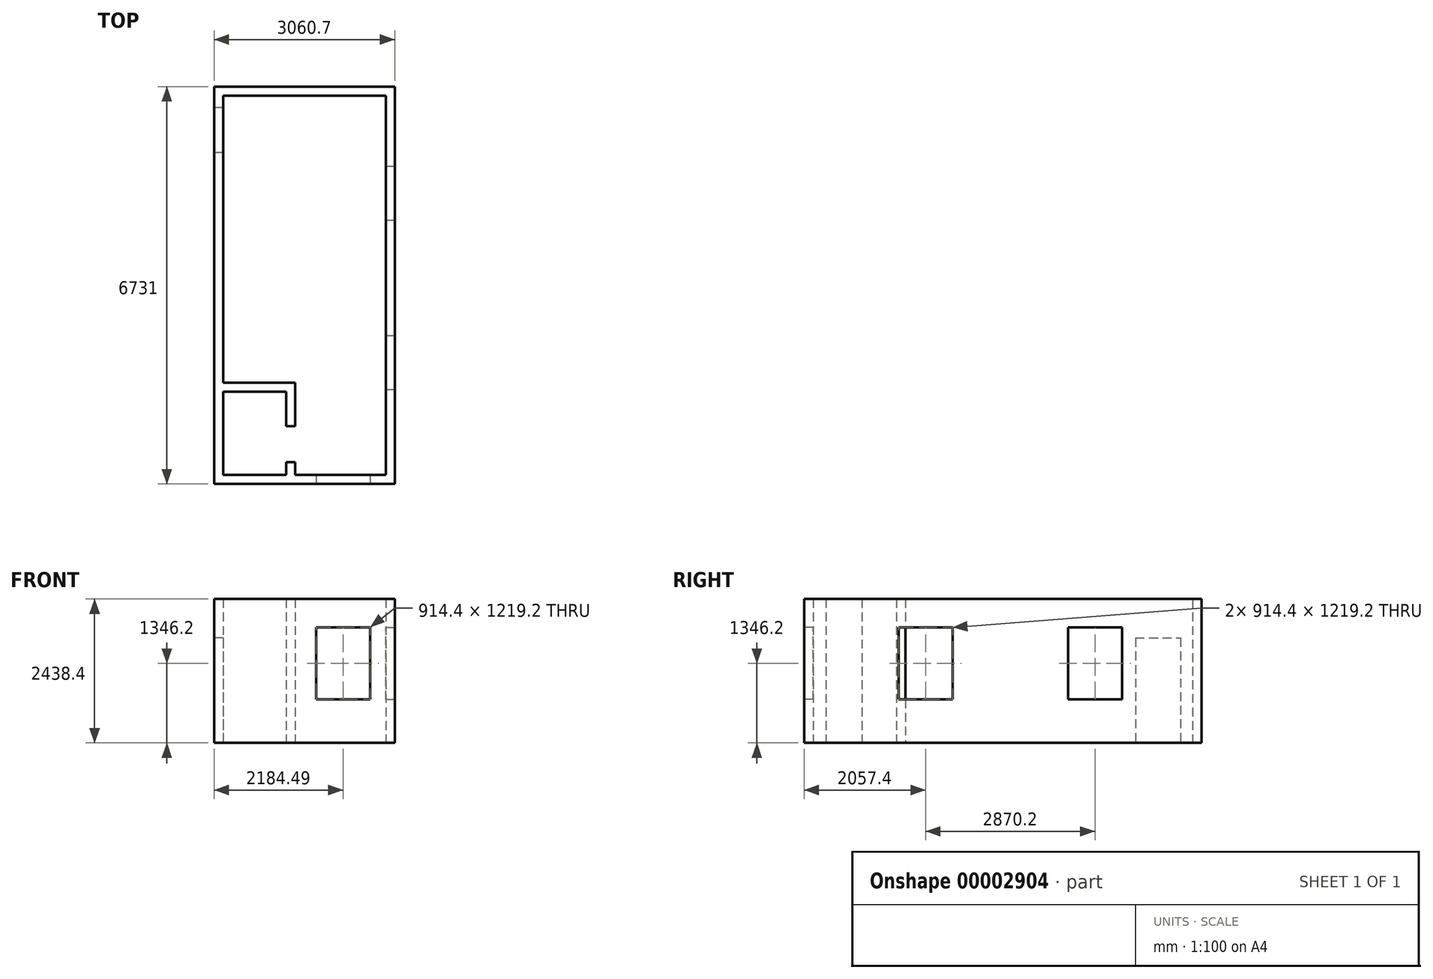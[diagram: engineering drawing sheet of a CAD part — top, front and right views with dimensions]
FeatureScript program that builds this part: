
annotation { "Feature Type Name" : "Feature", "Feature Type Description" : "" }
export const myFeature = defineFeature(function(context is Context, id is Id, definition is map)
    precondition{}
    {
        {
            var Q0;
            Q0=qCreatedBy(makeId("Top.planeOp"),FACE);
            var sketch = newSketch(context, id + "F0", { "sketchPlane" : qUnion([Q0])});
            skLineSegment(sketch, "E0", {"start": v(-1367.03, 42.73) * mm, "end": v(1388.87, 42.73) * mm});
            skLineSegment(sketch, "E1", {"start": v(1388.87, 42.73) * mm, "end": v(1388.87, -6383.47) * mm});
            skLineSegment(sketch, "E2", {"start": v(-1367.03, 42.73) * mm, "end": v(-1367.03, -160.47) * mm});
            skLineSegment(sketch, "E3", {"start": v(1388.87, -6383.47) * mm, "end": v(-147.83, -6383.47) * mm});
            skLineSegment(sketch, "E4.0", {"start": v(-1519.43, 195.13) * mm, "end": v(-1519.43, -160.47) * mm});
            skLineSegment(sketch, "E4.1", {"start": v(-1519.43, 195.13) * mm, "end": v(1541.27, 195.13) * mm});
            skLineSegment(sketch, "E4.2", {"start": v(1541.27, 195.13) * mm, "end": v(1541.27, -6535.87) * mm});
            skLineSegment(sketch, "E4.3", {"start": v(1541.27, -6535.87) * mm, "end": v(-1519.43, -6535.87) * mm});
            skLineSegment(sketch, "E5", {"start": v(-1519.43, -160.47) * mm, "end": v(-1367.03, -160.47) * mm});
            skLineSegment(sketch, "E6", {"start": v(-1519.43, -922.47) * mm, "end": v(-1367.03, -922.47) * mm});
            skLineSegment(sketch, "E7.trimOffspring", {"start": v(-1519.43, -922.47) * mm, "end": v(-1519.43, -6535.87) * mm});
            skLineSegment(sketch, "E8.trimOffspring", {"start": v(-1367.03, -922.47) * mm, "end": v(-1367.03, -4821.37) * mm});
            skLineSegment(sketch, "E9", {"start": v(-1367.03, -4821.37) * mm, "end": v(-147.83, -4821.37) * mm});
            skLineSegment(sketch, "E10", {"start": v(-147.83, -4821.37) * mm, "end": v(-147.83, -5557.97) * mm});
            skLineSegment(sketch, "E11.0", {"start": v(-300.23, -4973.77) * mm, "end": v(-300.23, -5557.97) * mm});
            skLineSegment(sketch, "E11.1", {"start": v(-1367.03, -4973.77) * mm, "end": v(-300.23, -4973.77) * mm});
            skLineSegment(sketch, "E12.trimOffspring", {"start": v(-1367.03, -4973.77) * mm, "end": v(-1367.03, -6383.47) * mm});
            skLineSegment(sketch, "E13.trimOffspring", {"start": v(-300.23, -6383.47) * mm, "end": v(-1367.03, -6383.47) * mm});
            skLineSegment(sketch, "E14", {"start": v(-300.23, -6167.57) * mm, "end": v(-147.83, -6167.57) * mm});
            skLineSegment(sketch, "E15", {"start": v(-147.83, -5557.97) * mm, "end": v(-300.23, -5557.97) * mm});
            skLineSegment(sketch, "E16.trimOffspring", {"start": v(-300.23, -6167.57) * mm, "end": v(-300.23, -6383.47) * mm});
            skLineSegment(sketch, "E17.trimOffspring", {"start": v(-147.83, -6167.57) * mm, "end": v(-147.83, -6383.47) * mm});
            skPoint(sketch, "E18.orphan", {"position": v(0, -5557.97) * mm});
            skPoint(sketch, "E19.orphan", {"position": v(0, -6167.57) * mm});
            skSolve(sketch);
        }
        {
            var Q0;
            Q0=makeQuery(id+"F0.imprint","IMPRINT",FACE,{"disambiguationData":[TD([[makeQuery(id+"F0.imprint","IMPRINT",EDGE,{"derivedFrom":sQuery(id+"F0.wireOp",EDGE,"E0")}),1.0]])]});
            extrude(context, id + "F1", {"entities" : qUnion([Q0]), "depth" : 2438.4 * mm});
        }
        {
            var Q0;
            Q0=makeQuery(id+"F1.opExtrude","SWEPT_FACE",FACE,{"disambiguationData":[OSD([sQuery(id+"F0.wireOp",EDGE,"E4.2")])]});
            var sketch = newSketch(context, id + "F2", { "sketchPlane" : qUnion([Q0])});
            skLineSegment(sketch, "E20.bottom", {"start": v(-1151.07, 1955.8) * mm, "end": v(-2065.47, 1955.8) * mm});
            skLineSegment(sketch, "E20.top", {"start": v(-1151.07, 736.6) * mm, "end": v(-2065.47, 736.6) * mm});
            skLineSegment(sketch, "E20.left", {"start": v(-1151.07, 1955.8) * mm, "end": v(-1151.07, 736.6) * mm});
            skLineSegment(sketch, "E20.right", {"start": v(-2065.47, 1955.8) * mm, "end": v(-2065.47, 736.6) * mm});
            skLineSegment(sketch, "E21.bottom", {"start": v(-4021.27, 1955.8) * mm, "end": v(-4935.67, 1955.8) * mm});
            skLineSegment(sketch, "E21.top", {"start": v(-4021.27, 736.6) * mm, "end": v(-4935.67, 736.6) * mm});
            skLineSegment(sketch, "E21.left", {"start": v(-4021.27, 1955.8) * mm, "end": v(-4021.27, 736.6) * mm});
            skLineSegment(sketch, "E21.right", {"start": v(-4935.67, 1955.8) * mm, "end": v(-4935.67, 736.6) * mm});
            skSolve(sketch);
        }
        {
            var Q0;
            Q0=makeQuery(id+"F2.imprint","IMPRINT",FACE,{"disambiguationData":[TD([[makeQuery(id+"F2.imprint","IMPRINT",EDGE,{"derivedFrom":sQuery(id+"F2.wireOp",EDGE,"E20.bottom")}),1.0]])]});
            var Q1;
            Q1=makeQuery(id+"F2.imprint","IMPRINT",FACE,{"disambiguationData":[TD([[makeQuery(id+"F2.imprint","IMPRINT",EDGE,{"derivedFrom":sQuery(id+"F2.wireOp",EDGE,"E21.bottom")}),1.0]])]});
            extrude(context, id + "F3", {"entities" : qUnion([Q0, Q1]), "operationType" : NewBodyOperationType.REMOVE, "endBound" : BoundingType.UP_TO_NEXT, "oppositeDirection" : true, "depth" : 25.4 * mm});
        }
        {
            var Q0;
            Q0=makeQuery(id+"F1.opExtrude","SWEPT_FACE",FACE,{"disambiguationData":[OSD([sQuery(id+"F0.wireOp",EDGE,"E4.3")])]});
            var sketch = newSketch(context, id + "F4", { "sketchPlane" : qUnion([Q0])});
            skLineSegment(sketch, "E22.bottom", {"start": v(207.86, 1955.8) * mm, "end": v(1122.26, 1955.8) * mm});
            skLineSegment(sketch, "E22.top", {"start": v(207.86, 736.6) * mm, "end": v(1122.26, 736.6) * mm});
            skLineSegment(sketch, "E22.left", {"start": v(207.86, 1955.8) * mm, "end": v(207.86, 736.6) * mm});
            skLineSegment(sketch, "E22.right", {"start": v(1122.26, 1955.8) * mm, "end": v(1122.26, 736.6) * mm});
            skSolve(sketch);
        }
        {
            var Q0;
            Q0 = qSketchRegion(id + "F4", true);
            extrude(context, id + "F5", {"entities" : qUnion([Q0]), "operationType" : NewBodyOperationType.REMOVE, "endBound" : BoundingType.UP_TO_NEXT, "oppositeDirection" : true, "depth" : 25.4 * mm});
        }
        {
            var Q0;
            Q0=makeQuery(id+"F1.opExtrude","SWEPT_FACE",FACE,{"disambiguationData":[OSD([sQuery(id+"F0.wireOp",EDGE,"E7.trimOffspring")])]});
            var sketch = newSketch(context, id + "F6", { "sketchPlane" : qUnion([Q0])});
            skLineSegment(sketch, "E23.bottom", {"start": v(922.47, 2438.4) * mm, "end": v(160.47, 2438.4) * mm});
            skLineSegment(sketch, "E23.top", {"start": v(922.47, 1778) * mm, "end": v(160.47, 1778) * mm});
            skLineSegment(sketch, "E23.left", {"start": v(922.47, 2438.4) * mm, "end": v(922.47, 1778) * mm});
            skLineSegment(sketch, "E23.right", {"start": v(160.47, 2438.4) * mm, "end": v(160.47, 1778) * mm});
            skSolve(sketch);
        }
        {
            var Q0;
            Q0 = qSketchRegion(id + "F6", true);
            extrude(context, id + "F7", {"entities" : qUnion([Q0]), "operationType" : NewBodyOperationType.ADD, "oppositeDirection" : true, "depth" : 152.4 * mm});
        }
    });
